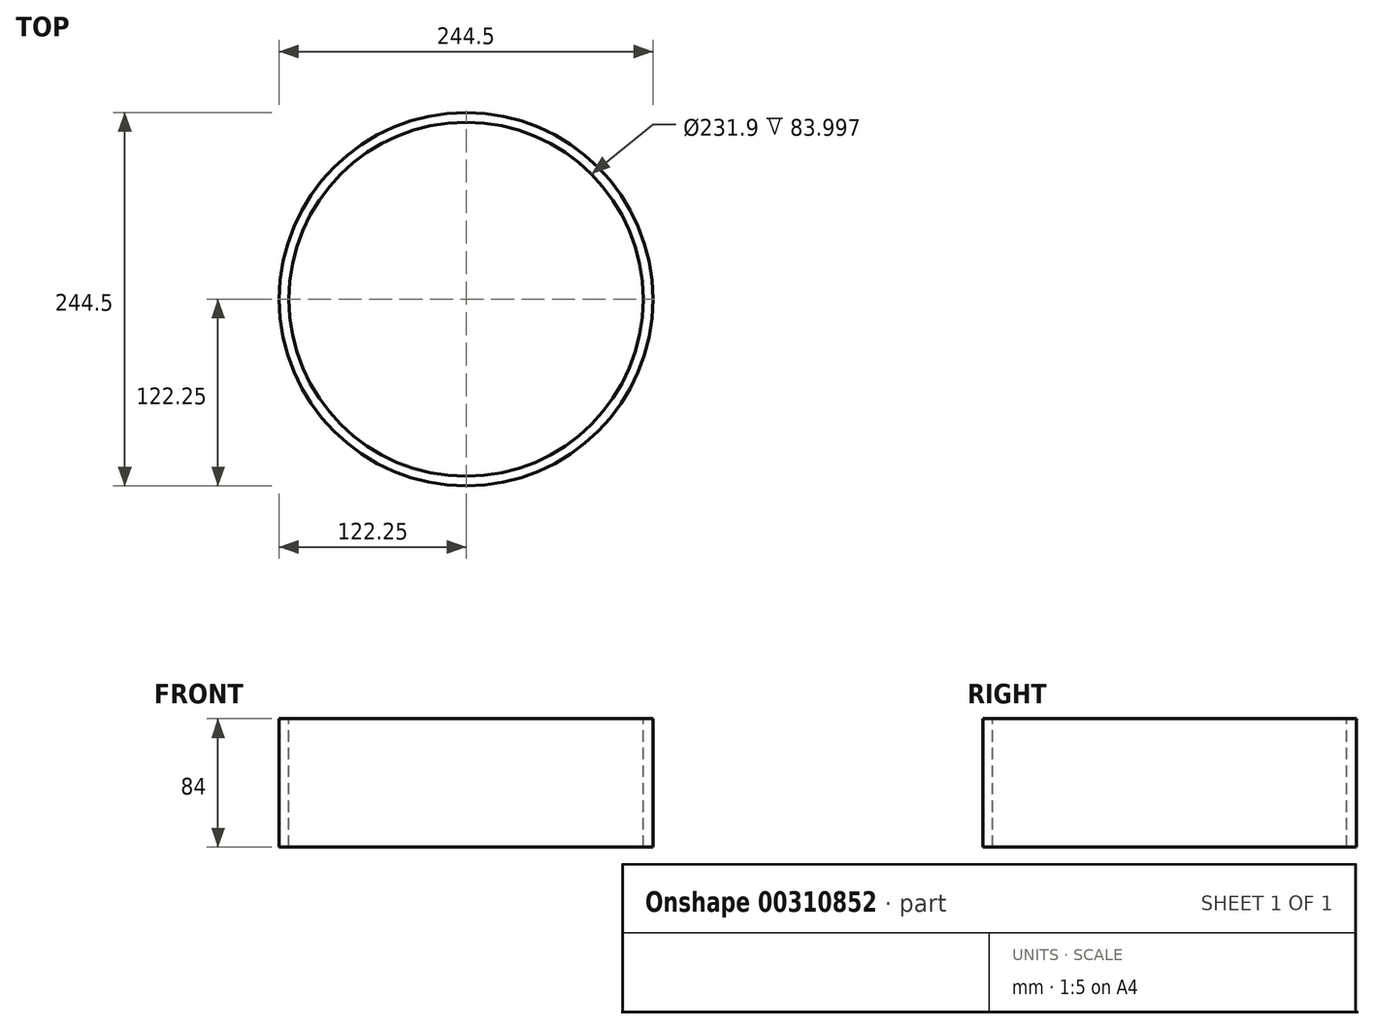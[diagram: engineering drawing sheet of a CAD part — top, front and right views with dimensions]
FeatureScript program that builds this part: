
annotation { "Feature Type Name" : "Feature", "Feature Type Description" : "" }
export const myFeature = defineFeature(function(context is Context, id is Id, definition is map)
    precondition{}
    {
        {
            var Q0;
            Q0=qCreatedBy(makeId("Front.planeOp"),FACE);
            var sketch = newSketch(context, id + "F0", { "sketchPlane" : qUnion([Q0])});
            skLineSegment(sketch, "E0", {"start": v(0, 11.86) * mm, "end": v(0, -78.14) * mm});
            skLineSegment(sketch, "E1", {"start": v(-115.95, -72.14) * mm, "end": v(-115.95, 11.86) * mm});
            skLineSegment(sketch, "E2", {"start": v(-115.95, 11.86) * mm, "end": v(-122.25, 11.86) * mm});
            skLineSegment(sketch, "E3", {"start": v(-122.25, 11.86) * mm, "end": v(-122.25, -72.14) * mm});
            skLineSegment(sketch, "E4", {"start": v(-122.25, -72.14) * mm, "end": v(-115.95, -72.14) * mm});
            skSolve(sketch);
        }
        {
            var Q0;
            Q0=makeQuery(id+"F0.imprint","IMPRINT",FACE,{"disambiguationData":[TD([[makeQuery(id+"F0.imprint","IMPRINT",EDGE,{"derivedFrom":sQuery(id+"F0.wireOp",EDGE,"E1")}),1.0]])]});
            var Q1;
            {var subQ1=sQuery(id+"F0.wireOp",EDGE,"bC3VX0uh-1GuJ-Sq3g-bcgl-Tm2HUiaqcZOy");Q1=makeQuery(id+"F0.imprint","IMPRINT",FACE,{"disambiguationData":[TD([[makeQuery(id+"F0.imprint","IMPRINT",EDGE,{"derivedFrom":subQ1}),1.0]])]});}
            var Q2;
            Q2=sQuery(id+"F0.wireOp",EDGE,"E0");
            revolve(context, id + "F1", {"entities" : qUnion([Q0, Q1]), "axis" : qUnion([Q2]), "revolveType" : RevolveType.FULL});
        }
    });
